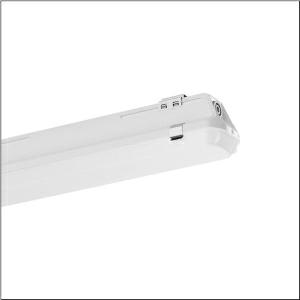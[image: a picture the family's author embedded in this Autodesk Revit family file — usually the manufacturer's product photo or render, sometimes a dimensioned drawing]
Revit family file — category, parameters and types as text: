
# Revit family: monsun_r__11_51fp20mp480h_c015
name_source: partatom
category: Lighting Fixtures
units: mm (PartAtom-declared; Revit-internal decimal feet)

## family parameters
Cut with Voids When Loaded = No
Host = Face
Light Source = No
Part Type = Normal
Room Calculation Point = No
Round Connector Dimension = Use Diameter
Shared = No

## types (1)
- --- (1 x LED, 8220 lm, 52.3 W, 4000K)
    Apparent Load = 52 VA
    CIE Flux Codes = 45 75 93 94 100
    Color Rendering = 80
    Color Temperature = 4000K
    Default Elevation = 1800 mm
    Description = Monsun® 11, damp-proof luminaire, chain hanger, primary optical cover: enclosure, of PC, light emission: direct distribution, primary light characteristic: symmetric, installation type: suspended mounting, surface-mounted, horizontal mounting, vertical mounting, LED, rated luminous flux: 8.220lm, luminous efficacy: 157lm/W, light colour: 840, colour temperature: 4000K, control gear: ON/OFF Multilumen, with terminal, 3-pole, max. 2.5mm², mains connection: 220..240V, AC, 50/60Hz, rated input power: 52W, luminaire housing, of glass-fibre reinforced polyester, uncoated, bright grey, incl. chain hanger, length: 1.590mm, width: 90mm, height: 88mm, clip for enclosure, of stainless steel (V2A), ceiling mounting element, of stainless steel (V2A), chain hanger, of stainless steel (V2A), protection rating (complete): IP66, insulation class (complete): insulation class I (protective earthing), certification: CE, ENEC, VDE, UKCA, protection symbol: D, impact resistance: IK08, permissible operating ambient temperature: -35..+40°C, standard: EN 50419, EN 60598-2-1, no direct snow, no direct sun, no direct rain, for indoor or canopied outdoor use, corresponds to IFS (International Featured Standards) requirements for safety and quality in the food industry, contact your sales advisor before using the luminaires in applications with unclear chemical exposure, large temperature fluctuations or condensation-forming humidity, LABS conformity tested according to VDMA 24364:2018-05, packaging unit: 1 piece
    Height = 89 mm
    Lamp = 1 x LED
    Lamp Light Flux = 8220 lm
    Lamp Power = 52.3 W
    Lamp count = 1
    Length = 1590 mm
    Luminous efficacy = 157 lm/W
    Manufacturer = Siteco
    ModVariant = No
    Model = 51FP20MP480H
    Mounting Place = Ceiling
    Mounting Type = Surface mounted
    Number of Poles = 1
    OnlyDefault = Yes
    Power Factor = 1
    Product Name = Monsun® 11
    Product group = damp-proof luminaire
    ProductGroupID = 301
    Protection Class = Protection class I
    Protection Degree = IP 66
    RLX_Detail_Level = 1
    RLX_Emergency_Light_Flux = 0 lm
    RLX_Emergency_Type = 0
    RLX_Emergency_Type_DB = No
    RlxData = <blob elided: 89997 chars, md5=c6537248>
    Socket = socket
    Standby Power = 0 W
    System Light Flux = 8220 lm
    System Power = 52 W
    Type Comments = factory setting: luminous flux: 100 % | (A | C | E) | 120 mA
    Type Image = l_1349237.jpg
    URL = http://relux.com
    VarID = @adj_199661
    Voltage = 0 V
    Weight = 0.00 kg
    Width = 90 mm

## geometry (parser evidence)
native form markers: Blend x4, Sweep x13
no freeform markers — native parametric forms only
